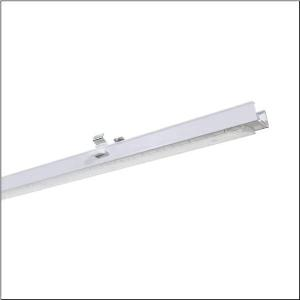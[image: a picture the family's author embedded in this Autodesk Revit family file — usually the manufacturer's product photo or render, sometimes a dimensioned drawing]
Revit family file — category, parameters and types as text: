
# Revit family: trunking_flex_31_51re12ma16b
name_source: partatom
category: Lighting Fixtures
units: mm (PartAtom-declared; Revit-internal decimal feet)

## family parameters
Cut with Voids When Loaded = No
Host = Face
Light Source = No
Part Type = Normal
Room Calculation Point = No
Round Connector Dimension = Use Diameter
Shared = No

## types (1)
- --- (1 x LED, 6400 lm, 40 W, 3500K)
    Apparent Load = 40 VA
    CIE Flux Codes = 65 91 98 99 100
    Color Rendering = 80
    Color Temperature = 3500K
    Default Elevation = 1800 mm
    Description = Trunking Flex 31, luminaire insert, of extruded aluminium section, coated, traffic white (RAL 9016), length: 1.172mm, width: 91mm, height: 53mm, LED rated luminous flux: 6.400lm, light colour: 835, SDCM (Standard Deviation of Colour Matching)MacAdam ≤ 3 SDCM (initial), control gear: ON/OFF Multilumen, with system connector: socket, mains connection: 220..240V, AC, 50/60Hz, rated input power: 40W, luminous flux adjustable on luminaire in four steps (3420/4540/5580/6630lm), connected load according to luminous flux setting (20/26/33/40W), primary light control with lens, of plastic, primary optical cover: cover, of PMMA, light emission: direct distribution, protection rating (complete): IP20, insulation class (complete): insulation class I (protective earthing), certification: CE, UKCA, impact resistance: IK02, permissible ambient temperature for indoor applications: -20..+40°C, packaging unit: 1 piece
    Height = 58 mm
    Lamp = 1 x LED
    Lamp Light Flux = 6400 lm
    Lamp Power = 40 W
    Lamp count = 1
    Length = 1172 mm
    Luminous efficacy = 160 lm/W
    Manufacturer = Siteco
    ModVariant = No
    Model = 51RE12MA16B
    Mounting Place = Ceiling
    Mounting Type = Pendant
    Number of Poles = 1
    OnlyDefault = Yes
    Power Factor = 1
    Product Name = Trunking Flex 31
    Product group = luminaire insert | ceiling pendant
    ProductGroupID = 901
    Protection Class = Protection class I
    Protection Degree = IP 20
    RLX_Detail_Level = 1
    RLX_Emergency_Light_Flux = 0 lm
    RLX_Emergency_Type = 0
    RLX_Emergency_Type_DB = No
    RlxData = <blob elided: 20061 chars, md5=0910af1e>
    Socket = socket
    Standby Power = 0 W
    System Light Flux = 6400 lm
    System Power = 40 W
    Type Comments = factory setting: luminous flux: 100 % | (ON | ON) | 300 mA
    Type Image = l_1266702.jpg
    URL = http://relux.com
    VarID = @adj_067139
    Voltage = 0 V
    Weight = 0.00 kg
    Width = 65 mm

## geometry (parser evidence)
native form markers: Blend x4, Sweep x11
no freeform markers — native parametric forms only
